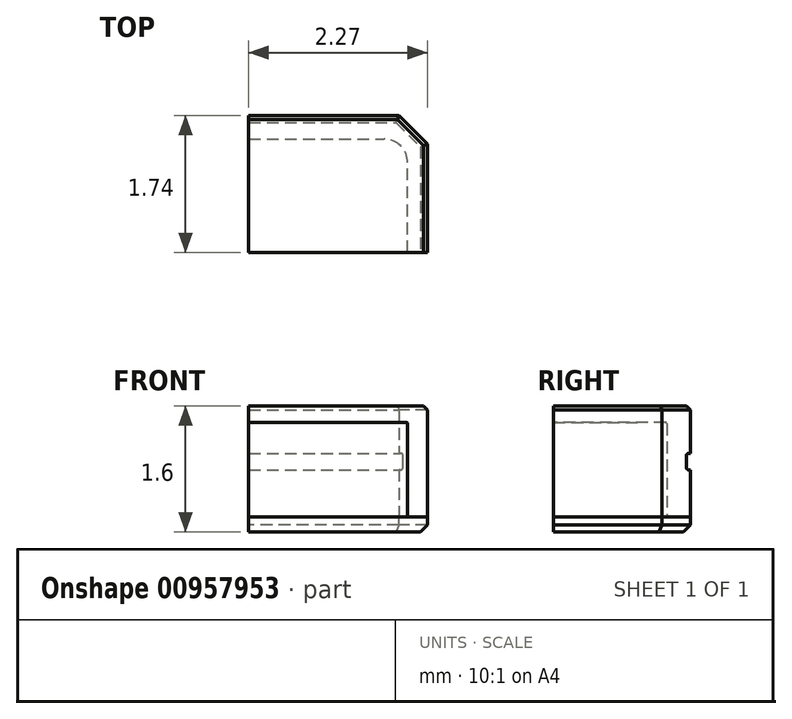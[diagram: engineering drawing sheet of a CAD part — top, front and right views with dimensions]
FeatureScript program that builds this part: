
annotation { "Feature Type Name" : "Feature", "Feature Type Description" : "" }
export const myFeature = defineFeature(function(context is Context, id is Id, definition is map)
    precondition{}
    {
        {
            var Q0;
            Q0=qCreatedBy(makeId("Top.planeOp"),FACE);
            var sketch = newSketch(context, id + "F0", { "sketchPlane" : qUnion([Q0])});
            skLineSegment(sketch, "E0.bottom", {"start": v(-2.27, 1.74) * mm, "end": v(2.27, 1.74) * mm});
            skLineSegment(sketch, "E0.top", {"start": v(-2.27, -1.74) * mm, "end": v(2.27, -1.74) * mm});
            skLineSegment(sketch, "E0.left", {"start": v(-2.27, 1.74) * mm, "end": v(-2.27, -1.74) * mm});
            skLineSegment(sketch, "E0.right", {"start": v(2.27, 1.74) * mm, "end": v(2.27, -1.74) * mm});
            skLineSegment(sketch, "E1", {"start": v(0, 2.06) * mm, "end": v(0, -3.31) * mm, "construction": true});
            skLineSegment(sketch, "E2", {"start": v(-2.87, 0) * mm, "end": v(4.16, 0) * mm, "construction": true});
            skSolve(sketch);
        }
        {
            var Q0;
            Q0=qSketchRegion(id+"F0",true);
            extrude(context, id + "F1", {"entities" : qUnion([Q0]), "oppositeDirection" : true, "depth" : 1.41 * mm, "offsetDistance" : 25 * mm});
        }
        {
            var Q0;
            Q0=makeQuery(id+"F1.opExtrude","SWEPT_EDGE",EDGE,{"disambiguationData":[OSD([sQuery(id+"F0.wireOp",EDGE,"E0.bottom"),sQuery(id+"F0.wireOp",EDGE,"E0.left")])]});
            var Q1;
            Q1=makeQuery(id+"F1.opExtrude","SWEPT_EDGE",EDGE,{"disambiguationData":[OSD([sQuery(id+"F0.wireOp",EDGE,"E0.top"),sQuery(id+"F0.wireOp",EDGE,"E0.left")])]});
            var Q2;
            Q2=makeQuery(id+"F1.opExtrude","SWEPT_EDGE",EDGE,{"disambiguationData":[OSD([sQuery(id+"F0.wireOp",EDGE,"E0.bottom"),sQuery(id+"F0.wireOp",EDGE,"E0.right")])]});
            var Q3;
            Q3=makeQuery(id+"F1.opExtrude","SWEPT_EDGE",EDGE,{"disambiguationData":[OSD([sQuery(id+"F0.wireOp",EDGE,"E0.top"),sQuery(id+"F0.wireOp",EDGE,"E0.right")])]});
            chamfer(context, id + "F2", {"entities" : qUnion([Q0, Q1, Q2, Q3]), "width" : 0.36 * mm, "tangentPropagation" : true});
        }
        {
            var Q0;
            Q0=makeQuery(id+"F1.opExtrude","CAP_EDGE",EDGE,{"disambiguationData":[OSD([sQuery(id+"F0.wireOp",EDGE,"E0.left")])],"isStart":true});
            var Q1;
            {var subQ0=sQuery(id+"F0.wireOp",EDGE,"E0.left");var subQ1=sQuery(id+"F0.wireOp",EDGE,"E0.bottom");Q1=makeQuery(id+"F2.opChamfer","BLEND_EDGE",EDGE,{"blendedFrom":[makeQuery(id+"F1.opExtrude","SWEPT_EDGE",EDGE,{"disambiguationData":[OSD([subQ1,subQ0])]}),makeQuery(id+"F1.opExtrude","CAP_FACE",FACE,{"disambiguationData":[OSD([subQ1,sQuery(id+"F0.wireOp",EDGE,"E0.top"),subQ0,sQuery(id+"F0.wireOp",EDGE,"E0.right")])],"isStart":true})],"blendedInto":[makeQuery(id+"F1.opExtrude","CAP_FACE",FACE,{"disambiguationData":[OSD([subQ1,sQuery(id+"F0.wireOp",EDGE,"E0.top"),subQ0,sQuery(id+"F0.wireOp",EDGE,"E0.right")])],"isStart":true})]});}
            var Q2;
            Q2=makeQuery(id+"F1.opExtrude","CAP_EDGE",EDGE,{"disambiguationData":[OSD([sQuery(id+"F0.wireOp",EDGE,"E0.bottom")])],"isStart":true});
            var Q3;
            {var subQ0=sQuery(id+"F0.wireOp",EDGE,"E0.right");var subQ1=sQuery(id+"F0.wireOp",EDGE,"E0.bottom");Q3=makeQuery(id+"F2.opChamfer","BLEND_EDGE",EDGE,{"blendedFrom":[makeQuery(id+"F1.opExtrude","SWEPT_EDGE",EDGE,{"disambiguationData":[OSD([subQ1,subQ0])]}),makeQuery(id+"F1.opExtrude","CAP_FACE",FACE,{"disambiguationData":[OSD([subQ1,sQuery(id+"F0.wireOp",EDGE,"E0.top"),sQuery(id+"F0.wireOp",EDGE,"E0.left"),subQ0])],"isStart":true})],"blendedInto":[makeQuery(id+"F1.opExtrude","CAP_FACE",FACE,{"disambiguationData":[OSD([subQ1,sQuery(id+"F0.wireOp",EDGE,"E0.top"),sQuery(id+"F0.wireOp",EDGE,"E0.left"),subQ0])],"isStart":true})]});}
            var Q4;
            Q4=makeQuery(id+"F1.opExtrude","CAP_EDGE",EDGE,{"disambiguationData":[OSD([sQuery(id+"F0.wireOp",EDGE,"E0.right")])],"isStart":true});
            var Q5;
            {var subQ0=sQuery(id+"F0.wireOp",EDGE,"E0.right");var subQ1=sQuery(id+"F0.wireOp",EDGE,"E0.top");Q5=makeQuery(id+"F2.opChamfer","BLEND_EDGE",EDGE,{"blendedFrom":[makeQuery(id+"F1.opExtrude","SWEPT_EDGE",EDGE,{"disambiguationData":[OSD([subQ1,subQ0])]}),makeQuery(id+"F1.opExtrude","CAP_FACE",FACE,{"disambiguationData":[OSD([sQuery(id+"F0.wireOp",EDGE,"E0.bottom"),subQ1,sQuery(id+"F0.wireOp",EDGE,"E0.left"),subQ0])],"isStart":true})],"blendedInto":[makeQuery(id+"F1.opExtrude","CAP_FACE",FACE,{"disambiguationData":[OSD([sQuery(id+"F0.wireOp",EDGE,"E0.bottom"),subQ1,sQuery(id+"F0.wireOp",EDGE,"E0.left"),subQ0])],"isStart":true})]});}
            var Q6;
            Q6=makeQuery(id+"F1.opExtrude","CAP_EDGE",EDGE,{"disambiguationData":[OSD([sQuery(id+"F0.wireOp",EDGE,"E0.top")])],"isStart":true});
            var Q7;
            {var subQ0=sQuery(id+"F0.wireOp",EDGE,"E0.left");var subQ1=sQuery(id+"F0.wireOp",EDGE,"E0.top");Q7=makeQuery(id+"F2.opChamfer","BLEND_EDGE",EDGE,{"blendedFrom":[makeQuery(id+"F1.opExtrude","SWEPT_EDGE",EDGE,{"disambiguationData":[OSD([subQ1,subQ0])]}),makeQuery(id+"F1.opExtrude","CAP_FACE",FACE,{"disambiguationData":[OSD([sQuery(id+"F0.wireOp",EDGE,"E0.bottom"),subQ1,subQ0,sQuery(id+"F0.wireOp",EDGE,"E0.right")])],"isStart":true})],"blendedInto":[makeQuery(id+"F1.opExtrude","CAP_FACE",FACE,{"disambiguationData":[OSD([sQuery(id+"F0.wireOp",EDGE,"E0.bottom"),subQ1,subQ0,sQuery(id+"F0.wireOp",EDGE,"E0.right")])],"isStart":true})]});}
            chamfer(context, id + "F3", {"entities" : qUnion([Q0, Q1, Q2, Q3, Q4, Q5, Q6, Q7]), "chamferType" : ChamferType.TWO_OFFSETS, "width1" : 0.05 * mm, "oppositeDirection" : false, "width2" : 0.05 * mm, "tangentPropagation" : true});
        }
        {
            var Q0;
            Q0=makeQuery(id+"F1.opExtrude","SWEPT_FACE",FACE,{"disambiguationData":[OSD([sQuery(id+"F0.wireOp",EDGE,"E0.right")])]});
            var sketch = newSketch(context, id + "F4", { "sketchPlane" : qUnion([Q0])});
            skLineSegment(sketch, "E3.bottom", {"start": v(-1.74, -0.6) * mm, "end": v(-1.72, -0.6) * mm});
            skLineSegment(sketch, "E3.top", {"start": v(-1.74, -0.81) * mm, "end": v(-1.72, -0.81) * mm});
            skLineSegment(sketch, "E3.left", {"start": v(-1.74, -0.6) * mm, "end": v(-1.74, -0.81) * mm});
            skLineSegment(sketch, "E3.right", {"start": v(-1.7, -0.63) * mm, "end": v(-1.7, -0.78) * mm});
            skPoint(sketch, "E4.visualSharp", {"position": v(-1.7, -0.6) * mm});
            skArc(sketch, "E4.filletArc", {"start": v(-1.7, -0.63) * mm, "mid": v(-1.7, -0.6) * mm, "end": v(-1.72, -0.6) * mm});
            skPoint(sketch, "E5.visualSharp", {"position": v(-1.7, -0.81) * mm});
            skArc(sketch, "E5.filletArc", {"start": v(-1.72, -0.81) * mm, "mid": v(-1.7, -0.8) * mm, "end": v(-1.7, -0.78) * mm});
            skLineSegment(sketch, "E6.MirrorCS", {"start": v(1.74, -0.6) * mm, "end": v(1.72, -0.6) * mm});
            skLineSegment(sketch, "E7.MirrorCS", {"start": v(1.74, -0.81) * mm, "end": v(1.72, -0.81) * mm});
            skArc(sketch, "E8.MirrorCS", {"start": v(1.72, -0.81) * mm, "mid": v(1.7, -0.8) * mm, "end": v(1.7, -0.78) * mm});
            skArc(sketch, "E9.MirrorCS", {"start": v(1.7, -0.63) * mm, "mid": v(1.7, -0.6) * mm, "end": v(1.72, -0.6) * mm});
            skPoint(sketch, "E10.MirrorP", {"position": v(1.7, -0.81) * mm});
            skLineSegment(sketch, "E11.MirrorCS", {"start": v(1.74, -0.6) * mm, "end": v(1.74, -0.81) * mm});
            skLineSegment(sketch, "E12.MirrorCS", {"start": v(1.7, -0.63) * mm, "end": v(1.7, -0.78) * mm});
            skPoint(sketch, "E13.MirrorP", {"position": v(1.7, -0.6) * mm});
            skSolve(sketch);
        }
        {
            var Q0;
            Q0=qSketchRegion(id+"F4",true);
            extrude(context, id + "F5", {"entities" : qUnion([Q0]), "operationType" : NewBodyOperationType.REMOVE, "endBound" : BoundingType.THROUGH_ALL, "oppositeDirection" : true, "depth" : 25 * mm, "offsetDistance" : 25 * mm});
        }
        {
            var Q0;
            Q0=makeQuery(id+"F1.opExtrude","CAP_FACE",FACE,{"disambiguationData":[OSD([sQuery(id+"F0.wireOp",EDGE,"E0.bottom"),sQuery(id+"F0.wireOp",EDGE,"E0.top"),sQuery(id+"F0.wireOp",EDGE,"E0.left"),sQuery(id+"F0.wireOp",EDGE,"E0.right")])],"isStart":false});
            var sketch = newSketch(context, id + "F6", { "sketchPlane" : qUnion([Q0])});
            skLineSegment(sketch, "E14.bottom", {"start": v(-1.72, 1.44) * mm, "end": v(1.72, 1.44) * mm});
            skLineSegment(sketch, "E14.top", {"start": v(-1.72, -1.44) * mm, "end": v(1.72, -1.44) * mm});
            skLineSegment(sketch, "E14.left", {"start": v(-2.02, 1.14) * mm, "end": v(-2.02, -1.14) * mm});
            skLineSegment(sketch, "E14.right", {"start": v(2.02, 1.14) * mm, "end": v(2.02, -1.14) * mm});
            skPoint(sketch, "E15.visualSharp", {"position": v(-2.02, 1.44) * mm});
            skArc(sketch, "E15.filletArc", {"start": v(-1.72, 1.44) * mm, "mid": v(-1.93, 1.35) * mm, "end": v(-2.02, 1.14) * mm});
            skPoint(sketch, "E16.visualSharp", {"position": v(2.02, 1.44) * mm});
            skArc(sketch, "E16.filletArc", {"start": v(2.02, 1.14) * mm, "mid": v(1.93, 1.35) * mm, "end": v(1.72, 1.44) * mm});
            skPoint(sketch, "E17.visualSharp", {"position": v(2.02, -1.44) * mm});
            skArc(sketch, "E17.filletArc", {"start": v(1.72, -1.44) * mm, "mid": v(1.93, -1.35) * mm, "end": v(2.02, -1.14) * mm});
            skPoint(sketch, "E18.visualSharp", {"position": v(-2.02, -1.44) * mm});
            skArc(sketch, "E18.filletArc", {"start": v(-2.02, -1.14) * mm, "mid": v(-1.93, -1.35) * mm, "end": v(-1.72, -1.44) * mm});
            skSolve(sketch);
        }
        {
            var Q0;
            Q0=qSketchRegion(id+"F6",true);
            extrude(context, id + "F7", {"entities" : qUnion([Q0]), "operationType" : NewBodyOperationType.REMOVE, "oppositeDirection" : true, "depth" : 1.2 * mm, "offsetDistance" : 25 * mm});
        }
        {
            var Q0;
            Q0=makeQuery(id+"F7.boolean.opBoolean","COPY",EDGE,{"derivedFrom":makeQuery(id+"F7.opExtrude","CAP_EDGE",EDGE,{"disambiguationData":[OSD([sQuery(id+"F6.wireOp",EDGE,"E14.top")])],"isStart":false})});
            var Q1;
            Q1=makeQuery(id+"F7.boolean.opBoolean","COPY",EDGE,{"derivedFrom":makeQuery(id+"F7.opExtrude","CAP_EDGE",EDGE,{"disambiguationData":[OSD([sQuery(id+"F6.wireOp",EDGE,"E17.filletArc")])],"isStart":false})});
            var Q2;
            Q2=makeQuery(id+"F7.boolean.opBoolean","COPY",EDGE,{"derivedFrom":makeQuery(id+"F7.opExtrude","CAP_EDGE",EDGE,{"disambiguationData":[OSD([sQuery(id+"F6.wireOp",EDGE,"E14.right")])],"isStart":false})});
            var Q3;
            Q3=makeQuery(id+"F7.boolean.opBoolean","COPY",EDGE,{"derivedFrom":makeQuery(id+"F7.opExtrude","CAP_EDGE",EDGE,{"disambiguationData":[OSD([sQuery(id+"F6.wireOp",EDGE,"E18.filletArc")])],"isStart":false})});
            var Q4;
            Q4=makeQuery(id+"F7.boolean.opBoolean","COPY",EDGE,{"derivedFrom":makeQuery(id+"F7.opExtrude","CAP_EDGE",EDGE,{"disambiguationData":[OSD([sQuery(id+"F6.wireOp",EDGE,"E16.filletArc")])],"isStart":false})});
            var Q5;
            Q5=makeQuery(id+"F7.boolean.opBoolean","COPY",EDGE,{"derivedFrom":makeQuery(id+"F7.opExtrude","CAP_EDGE",EDGE,{"disambiguationData":[OSD([sQuery(id+"F6.wireOp",EDGE,"E14.bottom")])],"isStart":false})});
            var Q6;
            Q6=makeQuery(id+"F7.boolean.opBoolean","COPY",EDGE,{"derivedFrom":makeQuery(id+"F7.opExtrude","CAP_EDGE",EDGE,{"disambiguationData":[OSD([sQuery(id+"F6.wireOp",EDGE,"E15.filletArc")])],"isStart":false})});
            var Q7;
            Q7=makeQuery(id+"F7.boolean.opBoolean","COPY",EDGE,{"derivedFrom":makeQuery(id+"F7.opExtrude","CAP_EDGE",EDGE,{"disambiguationData":[OSD([sQuery(id+"F6.wireOp",EDGE,"E14.left")])],"isStart":false})});
            fillet(context, id + "F8", {"entities" : qUnion([Q0, Q1, Q2, Q3, Q4, Q5, Q6, Q7]), "radius" : 0.01 * mm, "tangentPropagation" : true, "allowEdgeOverflow" : false});
        }
        {
            var Q0;
            Q0=makeQuery(id+"F1.opExtrude","CAP_FACE",FACE,{"disambiguationData":[OSD([sQuery(id+"F0.wireOp",EDGE,"E0.bottom"),sQuery(id+"F0.wireOp",EDGE,"E0.top"),sQuery(id+"F0.wireOp",EDGE,"E0.left"),sQuery(id+"F0.wireOp",EDGE,"E0.right")])],"isStart":false});
            var sketch = newSketch(context, id + "F9", { "sketchPlane" : qUnion([Q0])});
            skLineSegment(sketch, "E19.bottom", {"start": v(-1.9, 1.74) * mm, "end": v(1.91, 1.74) * mm});
            skLineSegment(sketch, "E19.top", {"start": v(-1.9, -1.74) * mm, "end": v(1.91, -1.74) * mm});
            skLineSegment(sketch, "E19.left", {"start": v(-2.27, 1.38) * mm, "end": v(-2.27, -1.38) * mm});
            skLineSegment(sketch, "E19.right", {"start": v(2.27, 1.38) * mm, "end": v(2.27, -1.38) * mm});
            skLineSegment(sketch, "E20", {"start": v(-1.9, 1.74) * mm, "end": v(-2.27, 1.38) * mm});
            skLineSegment(sketch, "E21", {"start": v(1.91, 1.74) * mm, "end": v(2.27, 1.38) * mm});
            skLineSegment(sketch, "E22", {"start": v(2.27, -1.38) * mm, "end": v(1.91, -1.74) * mm});
            skLineSegment(sketch, "E23", {"start": v(-2.27, -1.38) * mm, "end": v(-1.9, -1.74) * mm});
            skSolve(sketch);
        }
        {
            var Q0;
            Q0=qSketchRegion(id+"F9",true);
            extrude(context, id + "F10", {"entities" : qUnion([Q0]), "depth" : 0.19 * mm, "offsetDistance" : 25 * mm});
        }
        {
            var Q0;
            Q0=makeQuery(id+"F10.opExtrude","CAP_EDGE",EDGE,{"disambiguationData":[OSD([sQuery(id+"F9.wireOp",EDGE,"E19.left")])],"isStart":false});
            var Q1;
            Q1=makeQuery(id+"F10.opExtrude","CAP_EDGE",EDGE,{"disambiguationData":[OSD([sQuery(id+"F9.wireOp",EDGE,"E20")])],"isStart":false});
            var Q2;
            Q2=makeQuery(id+"F10.opExtrude","CAP_EDGE",EDGE,{"disambiguationData":[OSD([sQuery(id+"F9.wireOp",EDGE,"E19.bottom")])],"isStart":false});
            var Q3;
            Q3=makeQuery(id+"F10.opExtrude","CAP_EDGE",EDGE,{"disambiguationData":[OSD([sQuery(id+"F9.wireOp",EDGE,"E21")])],"isStart":false});
            var Q4;
            Q4=makeQuery(id+"F10.opExtrude","CAP_EDGE",EDGE,{"disambiguationData":[OSD([sQuery(id+"F9.wireOp",EDGE,"E19.right")])],"isStart":false});
            var Q5;
            Q5=makeQuery(id+"F10.opExtrude","CAP_EDGE",EDGE,{"disambiguationData":[OSD([sQuery(id+"F9.wireOp",EDGE,"E22")])],"isStart":false});
            var Q6;
            Q6=makeQuery(id+"F10.opExtrude","CAP_EDGE",EDGE,{"disambiguationData":[OSD([sQuery(id+"F9.wireOp",EDGE,"E19.top")])],"isStart":false});
            var Q7;
            Q7=makeQuery(id+"F10.opExtrude","CAP_EDGE",EDGE,{"disambiguationData":[OSD([sQuery(id+"F9.wireOp",EDGE,"E23")])],"isStart":false});
            chamfer(context, id + "F11", {"entities" : qUnion([Q0, Q1, Q2, Q3, Q4, Q5, Q6, Q7]), "width" : 0.09 * mm, "tangentPropagation" : true});
        }
        {
            var Q0;
            Q0=makeQuery(id+"F1.opExtrude","CAP_FACE",FACE,{"disambiguationData":[OSD([sQuery(id+"F0.wireOp",EDGE,"E0.bottom"),sQuery(id+"F0.wireOp",EDGE,"E0.top"),sQuery(id+"F0.wireOp",EDGE,"E0.left"),sQuery(id+"F0.wireOp",EDGE,"E0.right")])],"isStart":true});
            var sketch = newSketch(context, id + "F12", { "sketchPlane" : qUnion([Q0])});
            skLineSegment(sketch, "E24", {"start": v(0, 0) * mm, "end": v(0, 1.83) * mm});
            skLineSegment(sketch, "E25", {"start": v(0, 1.83) * mm, "end": v(-2.4, 1.83) * mm});
            skLineSegment(sketch, "E26", {"start": v(-2.4, 1.83) * mm, "end": v(-2.4, -2.34) * mm});
            skLineSegment(sketch, "E27", {"start": v(-2.4, -2.34) * mm, "end": v(2.94, -2.34) * mm});
            skLineSegment(sketch, "E28", {"start": v(2.94, -2.34) * mm, "end": v(2.94, 0) * mm});
            skLineSegment(sketch, "E29", {"start": v(2.94, 0) * mm, "end": v(0, 0) * mm});
            skSolve(sketch);
        }
        {
            var Q0;
            Q0 = qSketchRegion(id + "F12", true);
            extrude(context, id + "F13", {"entities" : qUnion([Q0]), "operationType" : NewBodyOperationType.REMOVE, "oppositeDirection" : true, "depth" : 25 * mm, "offsetDistance" : 25 * mm});
        }
    });
